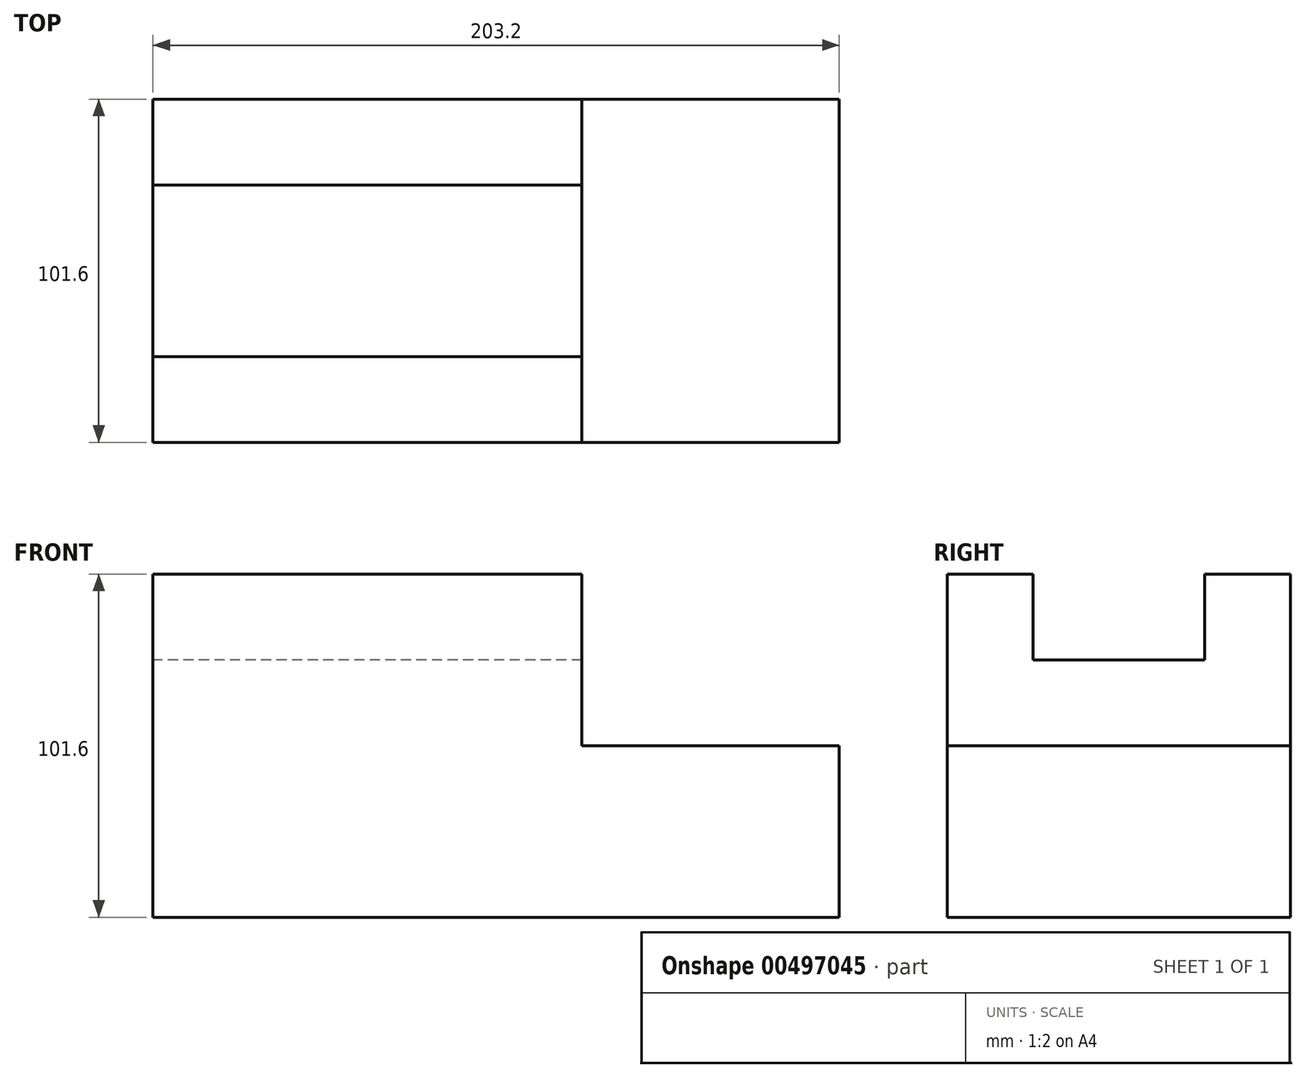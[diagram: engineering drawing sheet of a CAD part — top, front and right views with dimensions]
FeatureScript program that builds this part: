
annotation { "Feature Type Name" : "Feature", "Feature Type Description" : "" }
export const myFeature = defineFeature(function(context is Context, id is Id, definition is map)
    precondition{}
    {
        {
            var Q0;
            Q0=qCreatedBy(makeId("Front.planeOp"),FACE);
            var sketch = newSketch(context, id + "F0", { "sketchPlane" : qUnion([Q0])});
            skLineSegment(sketch, "E0", {"start": v(-151.6, -69.16) * mm, "end": v(51.6, -69.16) * mm});
            skLineSegment(sketch, "E1", {"start": v(51.6, -69.16) * mm, "end": v(51.6, -18.36) * mm});
            skLineSegment(sketch, "E2", {"start": v(51.6, -18.36) * mm, "end": v(-24.6, -18.36) * mm});
            skLineSegment(sketch, "E3", {"start": v(-24.6, -18.36) * mm, "end": v(-24.6, 32.44) * mm});
            skLineSegment(sketch, "E4", {"start": v(-24.6, 32.44) * mm, "end": v(-151.6, 32.44) * mm});
            skLineSegment(sketch, "E5", {"start": v(-151.6, 32.44) * mm, "end": v(-151.6, -69.16) * mm});
            skSolve(sketch);
        }
        {
            var Q0;
            Q0=makeQuery(id+"F0.imprint","IMPRINT",FACE,{"disambiguationData":[TD([[makeQuery(id+"F0.imprint","IMPRINT",EDGE,{"derivedFrom":sQuery(id+"F0.wireOp",EDGE,"E0")}),1.0]])]});
            extrude(context, id + "F1", {"entities" : qUnion([Q0]), "depth" : 101.6 * mm});
        }
        {
            var Q0;
            Q0=makeQuery(id+"F1.opExtrude","SWEPT_FACE",FACE,{"disambiguationData":[OSD([sQuery(id+"F0.wireOp",EDGE,"E4")])]});
            var sketch = newSketch(context, id + "F2", { "sketchPlane" : qUnion([Q0])});
            skLineSegment(sketch, "E6", {"start": v(-24.6, 0) * mm, "end": v(-24.6, -25.4) * mm});
            skLineSegment(sketch, "E7", {"start": v(-24.6, -101.6) * mm, "end": v(-24.6, -76.2) * mm});
            skLineSegment(sketch, "E8", {"start": v(-24.6, -76.2) * mm, "end": v(-24.6, -25.4) * mm});
            skLineSegment(sketch, "E9", {"start": v(-24.6, -25.4) * mm, "end": v(-151.6, -25.4) * mm});
            skLineSegment(sketch, "E10", {"start": v(-24.6, -76.2) * mm, "end": v(-151.6, -76.2) * mm});
            skLineSegment(sketch, "E11", {"start": v(-151.6, -76.2) * mm, "end": v(-151.6, -25.4) * mm});
            skSolve(sketch);
        }
        {
            var Q0;
            Q0=makeQuery(id+"F2.imprint","IMPRINT",FACE,{"disambiguationData":[TD([[makeQuery(id+"F2.imprint","IMPRINT",EDGE,{"derivedFrom":sQuery(id+"F2.wireOp",EDGE,"E8")}),1.0]])]});
            extrude(context, id + "F3", {"entities" : qUnion([Q0]), "operationType" : NewBodyOperationType.REMOVE, "oppositeDirection" : true, "depth" : 25.4 * mm});
        }
    });
